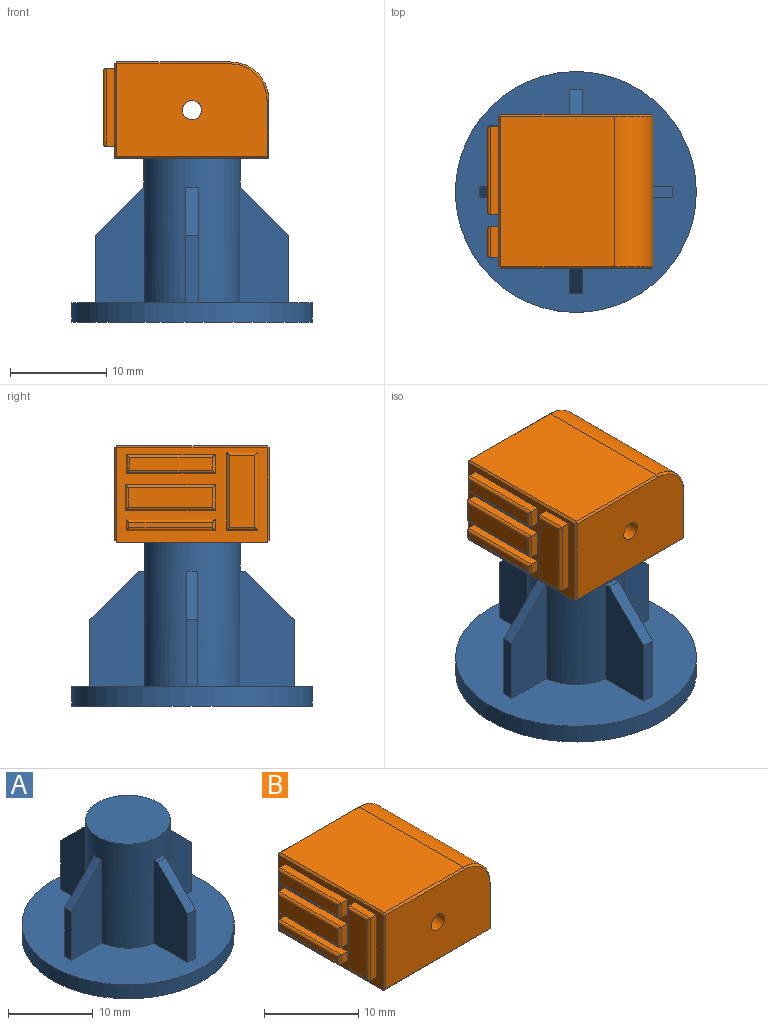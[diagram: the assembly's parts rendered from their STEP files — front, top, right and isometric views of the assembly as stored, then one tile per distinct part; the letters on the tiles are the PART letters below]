
ASSEMBLY  parts=2 mates=1
PART A: 27 faces, bbox 25x25x17 mm
  f0: plane 0.59x0.03mm, normal (0,0,1), area 0mm2, adj f2,f13,f22
  f1: plane 0.59x0.03mm, normal (0,0,1), area 0mm2, adj f2,f16,f20
  f2: cylinder r=5mm len=15mm, axis (0,0,-1), area 411.3mm2, adj f0,f1,f3,f4,f5,f7,f8,f9
  f3: plane 10x10mm, normal (0,0,1), area 78.5mm2, adj f2
  f4: plane 12x5.63mm, normal (-1,0,0), area 55.1mm2, adj f2,f6,f7,f21,f24
  f5: plane 12x5.63mm, normal (1,0,0), area 55.1mm2, adj f2,f6,f7,f21,f24
  f6: plane 7x1.32mm, normal (0,-1,0), area 9.2mm2, adj f4,f5,f21,f24
  f7: plane 1.32x0.63mm, normal (0,0,1), area 0.8mm2, adj f2,f4,f5,f21
  f8: plane 12x5.63mm, normal (1,0,0), area 55.1mm2, adj f2,f10,f11,f23,f24
  f9: plane 12x5.63mm, normal (-1,0,0), area 55.1mm2, adj f2,f10,f11,f23,f24
  f10: plane 7x1.32mm, normal (0,1,0), area 9.2mm2, adj f8,f9,f23,f24
  f11: plane 1.32x0.63mm, normal (0,0,1), area 0.8mm2, adj f2,f8,f9,f23
  f12: plane 12x5.03mm, normal (0,1,0), area 47.9mm2, adj f2,f14,f15,f22,f24
  f13: plane 12x5.03mm, normal (0,-1,0), area 47.9mm2, adj f0,f2,f14,f22,f24
  f14: plane 7x1.17mm, normal (1,0,0), area 8.2mm2, adj f12,f13,f22,f24
  f15: plane 0.59x0.03mm, normal (0,0,1), area 0mm2, adj f2,f12,f22
  f16: plane 12x5.03mm, normal (0,1,0), area 47.9mm2, adj f1,f2,f18,f20,f24
  f17: plane 12x5.03mm, normal (0,-1,0), area 47.9mm2, adj f2,f18,f19,f20,f24
  f18: plane 7x1.17mm, normal (-1,0,0), area 8.2mm2, adj f16,f17,f20,f24
  f19: plane 0.59x0.03mm, normal (0,0,1), area 0mm2, adj f2,f17,f20
  f20: plane 5x5mm, normal (-0.71,0,0.71), area 8.3mm2, adj f1,f16,f17,f18,f19
  f21: plane 5x5mm, normal (0,-0.71,0.71), area 9.3mm2, adj f4,f5,f6,f7
  f22: plane 5x5mm, normal (0.71,0,0.71), area 8.3mm2, adj f0,f12,f13,f14,f15
  f23: plane 5x5mm, normal (0,0.71,0.71), area 9.3mm2, adj f8,f9,f10,f11
  f24: plane 25x25mm, normal (0,0,1), area 385.8mm2, adj f2,f4,f5,f6,f8,f9,f10,f12
  f25: cylinder r=12.5mm len=25mm, axis (0,0,1), area 157.1mm2, adj f24,f26
  f26: plane 25x25mm, normal (0,0,-1), area 490.9mm2, adj f25
PART B: 57 faces, bbox 17.2x16x10 mm
  f0: plane 15.6x9.8mm, normal (-1,0,0), area 73.1mm2, adj f5,f7,f8,f9,f10,f12,f13,f14
  f1: plane 15.6x6mm, normal (1,0,0), area 93.6mm2, adj f5,f6,f43,f44
  f2: plane 15.6x9.6mm, normal (0,1,0), area 143.5mm2, adj f44,f47,f48,f51,f52,f56
  f3: plane 15.6x9.6mm, normal (0,-1,0), area 143.5mm2, adj f43,f45,f46,f49,f50,f56
  f4: plane 15.6x11.8mm, normal (0,0,1), area 184.1mm2, adj f6,f49,f52,f55
  f5: plane 16x15.6mm, normal (0,0,-1), area 249.6mm2, adj f0,f1,f46,f47
  f6: cylinder r=4mm len=15.6mm, axis (0,-1,0), area 98mm2, adj f1,f4,f45,f48
  f7: plane 1.95x0.9mm, normal (0,1,0), area 1.8mm2, adj f0,f8,f10,f40
  f8: plane 9.2x0.9mm, normal (0,0,-1), area 8.3mm2, adj f0,f7,f9,f42
  f9: plane 1.95x0.9mm, normal (0,-1,0), area 1.8mm2, adj f0,f8,f10,f41
  f10: plane 9.2x0.9mm, normal (0,0,1), area 8.3mm2, adj f0,f7,f9,f39
  f11: plane 8.6x1.35mm, normal (-1,0,0), area 11.6mm2, adj f39,f40,f41,f42
  f12: plane 2.65x0.9mm, normal (0,1,0), area 2.4mm2, adj f0,f13,f15,f35
  f13: plane 9.32x0.9mm, normal (0,0,-1), area 8.4mm2, adj f0,f12,f14,f37
  f14: plane 2.65x0.9mm, normal (0,-1,0), area 2.4mm2, adj f0,f13,f15,f38
  f15: plane 9.32x0.9mm, normal (0,0,1), area 8.4mm2, adj f0,f12,f14,f36
  f16: plane 8.72x2.05mm, normal (-1,0,0), area 17.9mm2, adj f35,f36,f37,f38
  f17: plane 1.18x0.9mm, normal (0,1,0), area 1.1mm2, adj f0,f18,f20,f32
  f18: plane 9.26x0.9mm, normal (0,0,-1), area 8.3mm2, adj f0,f17,f19,f34
  f19: plane 1.18x0.9mm, normal (0,-1,0), area 1.1mm2, adj f0,f18,f20,f33
  f20: plane 9.26x0.9mm, normal (0,0,1), area 8.3mm2, adj f0,f17,f19,f31
  f21: plane 8.66x0.58mm, normal (-1,0,0), area 5mm2, adj f31,f32,f33,f34
  f22: plane 8.08x0.9mm, normal (0,1,0), area 7.3mm2, adj f0,f23,f25,f28
  f23: plane 3.24x0.9mm, normal (0,0,-1), area 2.9mm2, adj f0,f22,f24,f30
  f24: plane 8.08x0.9mm, normal (0,-1,0), area 7.3mm2, adj f0,f23,f25,f29
  f25: plane 3.24x0.9mm, normal (0,0,1), area 2.9mm2, adj f0,f22,f24,f27
  f26: plane 7.48x2.64mm, normal (-1,0,0), area 19.8mm2, adj f27,f28,f29,f30
  f27: cylinder r=0.3mm len=3.24mm, axis (0,-1,0), area 1.4mm2, adj f25,f26,f28,f29
  f28: cylinder r=0.3mm len=8.08mm, axis (0,0,1), area 3.7mm2, adj f22,f26,f27,f30
  f29: cylinder r=0.3mm len=8.08mm, axis (0,0,-1), area 3.7mm2, adj f24,f26,f27,f30
  f30: cylinder r=0.3mm len=3.24mm, axis (0,1,0), area 1.4mm2, adj f23,f26,f28,f29
  f31: cylinder r=0.3mm len=9.26mm, axis (0,-1,0), area 4.3mm2, adj f20,f21,f32,f33
  f32: cylinder r=0.3mm len=1.18mm, axis (0,0,1), area 0.5mm2, adj f17,f21,f31,f34
  f33: cylinder r=0.3mm len=1.18mm, axis (0,0,-1), area 0.5mm2, adj f19,f21,f31,f34
  f34: cylinder r=0.3mm len=9.26mm, axis (0,1,0), area 4.3mm2, adj f18,f21,f32,f33
  f35: cylinder r=0.3mm len=2.65mm, axis (0,0,1), area 1.1mm2, adj f12,f16,f36,f37
  f36: cylinder r=0.3mm len=9.32mm, axis (0,-1,0), area 4.3mm2, adj f15,f16,f35,f38
  f37: cylinder r=0.3mm len=9.32mm, axis (0,1,0), area 4.3mm2, adj f13,f16,f35,f38
  f38: cylinder r=0.3mm len=2.65mm, axis (0,0,-1), area 1.1mm2, adj f14,f16,f36,f37
  f39: cylinder r=0.3mm len=9.2mm, axis (0,-1,0), area 4.2mm2, adj f10,f11,f40,f41
  f40: cylinder r=0.3mm len=1.95mm, axis (0,0,1), area 0.8mm2, adj f7,f11,f39,f42
  f41: cylinder r=0.3mm len=1.95mm, axis (0,0,-1), area 0.8mm2, adj f9,f11,f39,f42
  f42: cylinder r=0.3mm len=9.2mm, axis (0,1,0), area 4.2mm2, adj f8,f11,f40,f41
  f43: plane 6x0.2mm, normal (0.71,-0.71,0), area 1.7mm2, adj f1,f3,f45,f46
  f44: plane 6x0.2mm, normal (0.71,0.71,0), area 1.7mm2, adj f1,f2,f47,f48
  f45: cone r=3.8mm half-angle=45deg, axis (0,1,0), area 1.7mm2, adj f3,f6,f43,f49
  f46: plane 16x0.2mm, normal (0,-0.71,-0.71), area 4.5mm2, adj f3,f5,f43,f50
  f47: plane 16x0.2mm, normal (0,0.71,-0.71), area 4.5mm2, adj f2,f5,f44,f51
  f48: cone r=3.8mm half-angle=45deg, axis (0,-1,0), area 1.7mm2, adj f2,f6,f44,f52
  f49: plane 11.8x0.2mm, normal (0,-0.71,0.71), area 3.3mm2, adj f3,f4,f45,f53
  f50: plane 9.8x0.2mm, normal (-0.71,-0.71,0), area 2.7mm2, adj f0,f3,f46,f53
  f51: plane 9.8x0.2mm, normal (-0.71,0.71,0), area 2.7mm2, adj f0,f2,f47,f54
  f52: plane 11.8x0.2mm, normal (0,0.71,0.71), area 3.3mm2, adj f2,f4,f48,f54
  f53: plane 0.2x0.2mm, normal (-0.58,-0.58,0.58), area 0mm2, adj f49,f50,f55
  f54: plane 0.2x0.2mm, normal (-0.58,0.58,0.58), area 0mm2, adj f51,f52,f55
  f55: plane 15.6x0.2mm, normal (-0.71,0,0.71), area 4.4mm2, adj f0,f4,f53,f54
  f56: cylinder r=1mm len=16mm, axis (0,-1,0), area 100.5mm2, adj f2,f3
PLACE A t=(-0.46,0.92,7.47)mm
PLACE B t=(-0.46,0.92,22.47)mm
MATE fastened A.f2 <-> B.f5  axis (0,0,1) through (-0.46,0.92,22.47)mm
